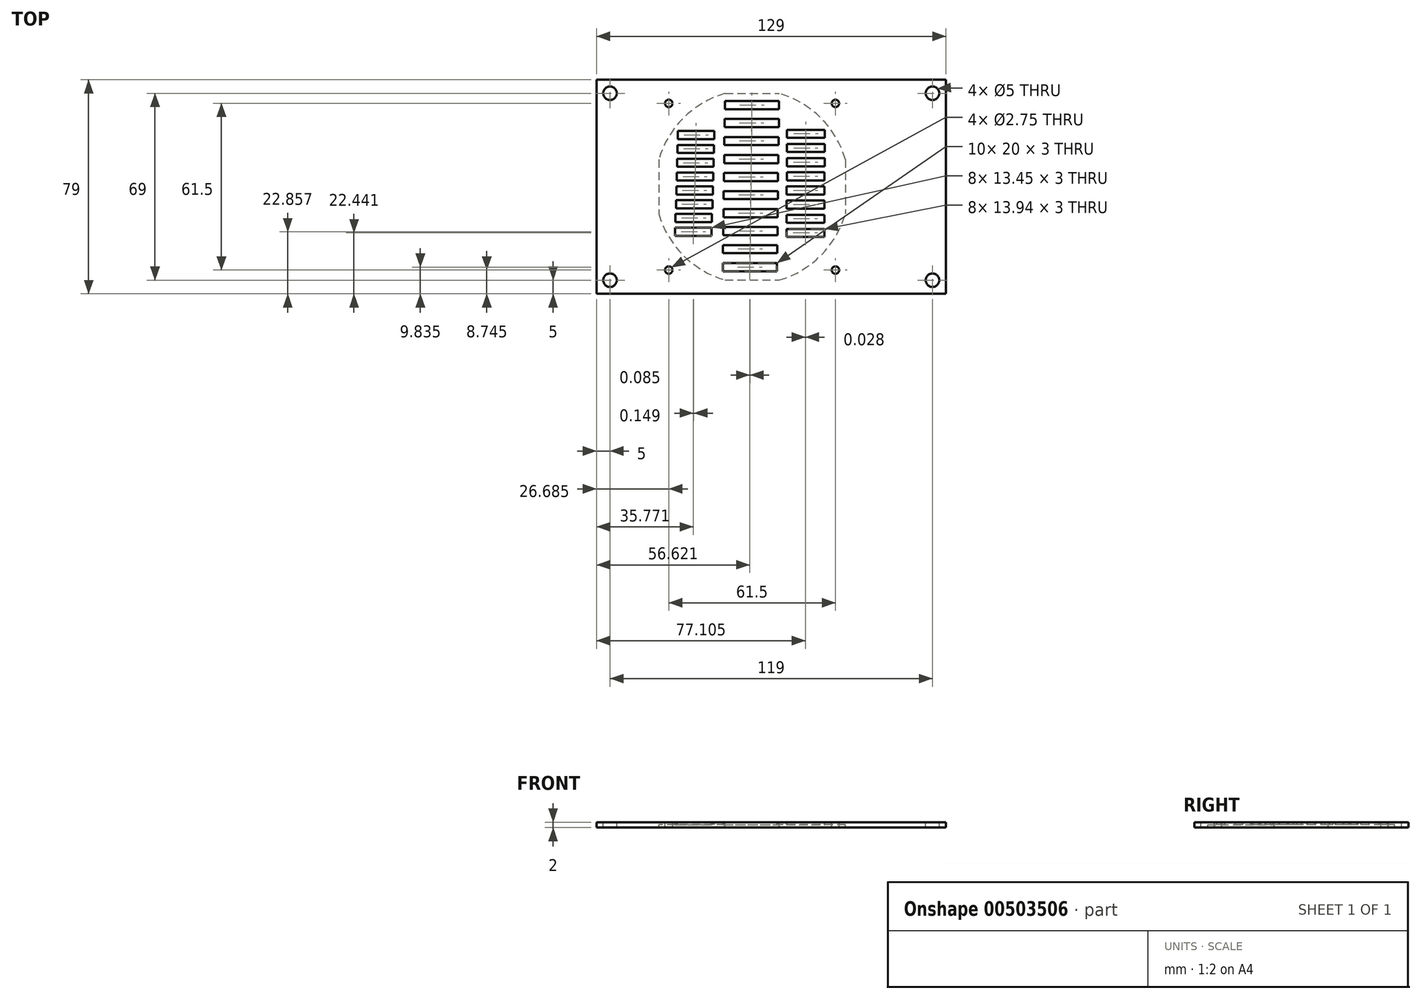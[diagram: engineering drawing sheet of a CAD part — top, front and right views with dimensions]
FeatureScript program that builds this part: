
annotation { "Feature Type Name" : "Feature", "Feature Type Description" : "" }
export const myFeature = defineFeature(function(context is Context, id is Id, definition is map)
    precondition{}
    {
        {
            var Q0;
            Q0=qCreatedBy(makeId("Top.planeOp"),FACE);
            var sketch = newSketch(context, id + "F0", { "sketchPlane" : qUnion([Q0])});
            skLineSegment(sketch, "E0.bottom", {"start": v(0, 0) * mm, "end": v(129, 0) * mm});
            skLineSegment(sketch, "E0.top", {"start": v(0, 79) * mm, "end": v(129, 79) * mm});
            skLineSegment(sketch, "E0.left", {"start": v(0, 0) * mm, "end": v(0, 79) * mm});
            skLineSegment(sketch, "E0.right", {"start": v(129, 0) * mm, "end": v(129, 79) * mm});
            skCircle(sketch, "E1", {"center": v(5, 74) * mm, "radius": 2.5 * mm});
            skCircle(sketch, "E2", {"center": v(124, 74) * mm, "radius": 2.5 * mm});
            skCircle(sketch, "E3", {"center": v(124, 5) * mm, "radius": 2.5 * mm});
            skCircle(sketch, "E4", {"center": v(5, 5) * mm, "radius": 2.5 * mm});
            skLineSegment(sketch, "E5.bottom", {"start": v(47.43, 73.93) * mm, "end": v(67.44, 73.93) * mm});
            skLineSegment(sketch, "E5.top", {"start": v(47.43, 5.06) * mm, "end": v(67.44, 5.06) * mm});
            skLineSegment(sketch, "E5.left", {"start": v(23, 49.5) * mm, "end": v(23, 29.49) * mm});
            skLineSegment(sketch, "E5.right", {"start": v(93.24, 41.52) * mm, "end": v(93.24, 41.52) * mm});
            skArc(sketch, "E6", {"start": v(23, 29.49) * mm, "mid": v(32.08, 14.14) * mm, "end": v(47.43, 5.06) * mm});
            skArc(sketch, "E7.trimOffspring", {"start": v(91.87, 49.5) * mm, "mid": v(82.8, 64.85) * mm, "end": v(67.44, 73.93) * mm});
            skArc(sketch, "E8.trimOffspring", {"start": v(47.43, 73.93) * mm, "mid": v(32.08, 64.85) * mm, "end": v(23, 49.5) * mm});
            skArc(sketch, "E9.trimOffspring", {"start": v(67.44, 5.06) * mm, "mid": v(82.8, 14.14) * mm, "end": v(91.87, 29.49) * mm});
            skLineSegment(sketch, "E10.bottom", {"start": v(16.58, 79) * mm, "end": v(98.29, 79) * mm});
            skLineSegment(sketch, "E10.top", {"start": v(16.58, 0) * mm, "end": v(98.29, 0) * mm});
            skLineSegment(sketch, "E10.left", {"start": v(16.58, 79) * mm, "end": v(16.58, 0) * mm});
            skLineSegment(sketch, "E10.right", {"start": v(98.29, 79) * mm, "end": v(98.29, 0) * mm});
            skCircle(sketch, "E11", {"center": v(26.68, 70.25) * mm, "radius": 1.38 * mm});
            skCircle(sketch, "E12", {"center": v(88.18, 70.25) * mm, "radius": 1.38 * mm});
            skCircle(sketch, "E13", {"center": v(88.19, 8.75) * mm, "radius": 1.38 * mm});
            skCircle(sketch, "E14", {"center": v(26.68, 8.75) * mm, "radius": 1.38 * mm});
            skPoint(sketch, "E15.firstSnap0", {"position": v(32.08, 14.14) * mm});
            skPoint(sketch, "E15.oppositeSnap0", {"position": v(86.71, 18.79) * mm});
            skLineSegment(sketch, "E16", {"start": v(91.87, 49.5) * mm, "end": v(91.87, 29.49) * mm});
            skLineSegment(sketch, "E17.bottom", {"start": v(47.38, 71.15) * mm, "end": v(67.38, 71.15) * mm});
            skLineSegment(sketch, "E17.top", {"start": v(47.38, 68.15) * mm, "end": v(67.38, 68.15) * mm});
            skLineSegment(sketch, "E17.left", {"start": v(47.38, 71.15) * mm, "end": v(47.38, 68.15) * mm});
            skLineSegment(sketch, "E17.right", {"start": v(67.38, 71.15) * mm, "end": v(67.38, 68.15) * mm});
            skLineSegment(sketch, "E18.1.0.0", {"start": v(47.3, 64.5) * mm, "end": v(67.3, 64.5) * mm});
            skLineSegment(sketch, "E18.1.0.1", {"start": v(47.3, 61.5) * mm, "end": v(67.3, 61.5) * mm});
            skLineSegment(sketch, "E18.1.0.2", {"start": v(47.3, 64.5) * mm, "end": v(47.3, 61.5) * mm});
            skLineSegment(sketch, "E18.1.0.3", {"start": v(67.3, 64.5) * mm, "end": v(67.3, 61.5) * mm});
            skLineSegment(sketch, "E18.2.0.0", {"start": v(47.22, 57.85) * mm, "end": v(67.22, 57.85) * mm});
            skLineSegment(sketch, "E18.2.0.1", {"start": v(47.22, 54.85) * mm, "end": v(67.22, 54.85) * mm});
            skLineSegment(sketch, "E18.2.0.2", {"start": v(47.22, 57.85) * mm, "end": v(47.22, 54.85) * mm});
            skLineSegment(sketch, "E18.2.0.3", {"start": v(67.22, 57.85) * mm, "end": v(67.22, 54.85) * mm});
            skLineSegment(sketch, "E18.3.0.0", {"start": v(47.13, 51.2) * mm, "end": v(67.13, 51.2) * mm});
            skLineSegment(sketch, "E18.3.0.1", {"start": v(47.13, 48.2) * mm, "end": v(67.13, 48.2) * mm});
            skLineSegment(sketch, "E18.3.0.2", {"start": v(47.13, 51.2) * mm, "end": v(47.13, 48.2) * mm});
            skLineSegment(sketch, "E18.3.0.3", {"start": v(67.13, 51.2) * mm, "end": v(67.13, 48.2) * mm});
            skLineSegment(sketch, "E18.4.0.0", {"start": v(47.05, 44.56) * mm, "end": v(67.05, 44.56) * mm});
            skLineSegment(sketch, "E18.4.0.1", {"start": v(47.05, 41.56) * mm, "end": v(67.05, 41.56) * mm});
            skLineSegment(sketch, "E18.4.0.2", {"start": v(47.05, 44.56) * mm, "end": v(47.05, 41.56) * mm});
            skLineSegment(sketch, "E18.4.0.3", {"start": v(67.05, 44.56) * mm, "end": v(67.05, 41.56) * mm});
            skLineSegment(sketch, "E18.5.0.0", {"start": v(46.96, 37.92) * mm, "end": v(66.96, 37.92) * mm});
            skLineSegment(sketch, "E18.5.0.1", {"start": v(46.96, 34.92) * mm, "end": v(66.96, 34.92) * mm});
            skLineSegment(sketch, "E18.5.0.2", {"start": v(46.96, 37.92) * mm, "end": v(46.96, 34.92) * mm});
            skLineSegment(sketch, "E18.5.0.3", {"start": v(66.96, 37.92) * mm, "end": v(66.96, 34.92) * mm});
            skLineSegment(sketch, "E18.6.0.0", {"start": v(46.88, 31.27) * mm, "end": v(66.88, 31.27) * mm});
            skLineSegment(sketch, "E18.6.0.1", {"start": v(46.88, 28.27) * mm, "end": v(66.88, 28.27) * mm});
            skLineSegment(sketch, "E18.6.0.2", {"start": v(46.88, 31.27) * mm, "end": v(46.88, 28.27) * mm});
            skLineSegment(sketch, "E18.6.0.3", {"start": v(66.88, 31.27) * mm, "end": v(66.88, 28.27) * mm});
            skLineSegment(sketch, "E18.7.0.0", {"start": v(46.8, 24.63) * mm, "end": v(66.8, 24.63) * mm});
            skLineSegment(sketch, "E18.7.0.1", {"start": v(46.8, 21.63) * mm, "end": v(66.8, 21.63) * mm});
            skLineSegment(sketch, "E18.7.0.2", {"start": v(46.8, 24.63) * mm, "end": v(46.8, 21.63) * mm});
            skLineSegment(sketch, "E18.7.0.3", {"start": v(66.8, 24.63) * mm, "end": v(66.8, 21.63) * mm});
            skLineSegment(sketch, "E18.8.0.0", {"start": v(46.7, 17.98) * mm, "end": v(66.7, 17.98) * mm});
            skLineSegment(sketch, "E18.8.0.1", {"start": v(46.7, 14.98) * mm, "end": v(66.7, 14.98) * mm});
            skLineSegment(sketch, "E18.8.0.2", {"start": v(46.7, 17.98) * mm, "end": v(46.7, 14.98) * mm});
            skLineSegment(sketch, "E18.8.0.3", {"start": v(66.7, 17.98) * mm, "end": v(66.7, 14.98) * mm});
            skLineSegment(sketch, "E18.9.0.0", {"start": v(46.62, 11.34) * mm, "end": v(66.62, 11.34) * mm});
            skLineSegment(sketch, "E18.9.0.1", {"start": v(46.62, 8.34) * mm, "end": v(66.62, 8.34) * mm});
            skLineSegment(sketch, "E18.9.0.2", {"start": v(46.62, 11.34) * mm, "end": v(46.62, 8.34) * mm});
            skLineSegment(sketch, "E18.9.0.3", {"start": v(66.62, 11.34) * mm, "end": v(66.62, 8.34) * mm});
            skLineSegment(sketch, "E18.direction1", {"start": v(47.38, 68.15) * mm, "end": v(47.3, 61.5) * mm, "construction": true});
            skLineSegment(sketch, "E19.bottom", {"start": v(30.09, 60.04) * mm, "end": v(43.54, 60.04) * mm});
            skLineSegment(sketch, "E19.top", {"start": v(30.09, 57.04) * mm, "end": v(43.54, 57.04) * mm});
            skLineSegment(sketch, "E19.left", {"start": v(30.09, 60.04) * mm, "end": v(30.09, 57.04) * mm});
            skLineSegment(sketch, "E19.right", {"start": v(43.54, 60.04) * mm, "end": v(43.54, 57.04) * mm});
            skLineSegment(sketch, "E20.1.0.0", {"start": v(29.94, 51.94) * mm, "end": v(43.39, 51.94) * mm});
            skLineSegment(sketch, "E20.1.0.1", {"start": v(29.94, 54.94) * mm, "end": v(43.39, 54.94) * mm});
            skLineSegment(sketch, "E20.1.0.2", {"start": v(43.39, 54.94) * mm, "end": v(43.39, 51.94) * mm});
            skLineSegment(sketch, "E20.1.0.3", {"start": v(29.94, 54.94) * mm, "end": v(29.94, 51.94) * mm});
            skLineSegment(sketch, "E20.2.0.0", {"start": v(29.79, 46.85) * mm, "end": v(43.24, 46.85) * mm});
            skLineSegment(sketch, "E20.2.0.1", {"start": v(29.79, 49.85) * mm, "end": v(43.24, 49.85) * mm});
            skLineSegment(sketch, "E20.2.0.2", {"start": v(43.24, 49.85) * mm, "end": v(43.24, 46.85) * mm});
            skLineSegment(sketch, "E20.2.0.3", {"start": v(29.79, 49.85) * mm, "end": v(29.79, 46.85) * mm});
            skLineSegment(sketch, "E20.3.0.0", {"start": v(29.64, 41.75) * mm, "end": v(43.1, 41.75) * mm});
            skLineSegment(sketch, "E20.3.0.1", {"start": v(29.64, 44.75) * mm, "end": v(43.1, 44.75) * mm});
            skLineSegment(sketch, "E20.3.0.2", {"start": v(43.1, 44.75) * mm, "end": v(43.1, 41.75) * mm});
            skLineSegment(sketch, "E20.3.0.3", {"start": v(29.64, 44.75) * mm, "end": v(29.64, 41.75) * mm});
            skLineSegment(sketch, "E20.4.0.0", {"start": v(29.5, 36.65) * mm, "end": v(42.94, 36.65) * mm});
            skLineSegment(sketch, "E20.4.0.1", {"start": v(29.5, 39.65) * mm, "end": v(42.94, 39.65) * mm});
            skLineSegment(sketch, "E20.4.0.2", {"start": v(42.94, 39.65) * mm, "end": v(42.94, 36.65) * mm});
            skLineSegment(sketch, "E20.4.0.3", {"start": v(29.5, 39.65) * mm, "end": v(29.5, 36.65) * mm});
            skLineSegment(sketch, "E20.5.0.0", {"start": v(29.34, 31.55) * mm, "end": v(42.8, 31.55) * mm});
            skLineSegment(sketch, "E20.5.0.1", {"start": v(29.34, 34.55) * mm, "end": v(42.8, 34.55) * mm});
            skLineSegment(sketch, "E20.5.0.2", {"start": v(42.8, 34.55) * mm, "end": v(42.8, 31.55) * mm});
            skLineSegment(sketch, "E20.5.0.3", {"start": v(29.34, 34.55) * mm, "end": v(29.34, 31.55) * mm});
            skLineSegment(sketch, "E20.6.0.0", {"start": v(29.2, 26.45) * mm, "end": v(42.65, 26.45) * mm});
            skLineSegment(sketch, "E20.6.0.1", {"start": v(29.2, 29.45) * mm, "end": v(42.65, 29.45) * mm});
            skLineSegment(sketch, "E20.6.0.2", {"start": v(42.65, 29.45) * mm, "end": v(42.65, 26.45) * mm});
            skLineSegment(sketch, "E20.6.0.3", {"start": v(29.2, 29.45) * mm, "end": v(29.2, 26.45) * mm});
            skLineSegment(sketch, "E20.7.0.0", {"start": v(29.04, 21.36) * mm, "end": v(42.5, 21.36) * mm});
            skLineSegment(sketch, "E20.7.0.1", {"start": v(29.04, 24.36) * mm, "end": v(42.5, 24.36) * mm});
            skLineSegment(sketch, "E20.7.0.2", {"start": v(42.5, 24.36) * mm, "end": v(42.5, 21.36) * mm});
            skLineSegment(sketch, "E20.7.0.3", {"start": v(29.04, 24.36) * mm, "end": v(29.04, 21.36) * mm});
            skLineSegment(sketch, "E20.direction1", {"start": v(30.09, 57.04) * mm, "end": v(29.94, 51.94) * mm, "construction": true});
            skLineSegment(sketch, "E21.bottom", {"start": v(70.33, 60.53) * mm, "end": v(84.27, 60.53) * mm});
            skLineSegment(sketch, "E21.top", {"start": v(70.33, 57.53) * mm, "end": v(84.27, 57.53) * mm});
            skLineSegment(sketch, "E21.left", {"start": v(70.33, 60.53) * mm, "end": v(70.33, 57.53) * mm});
            skLineSegment(sketch, "E21.right", {"start": v(84.27, 60.53) * mm, "end": v(84.27, 57.53) * mm});
            skLineSegment(sketch, "E22.1.0.0", {"start": v(84.24, 55.3) * mm, "end": v(84.24, 52.3) * mm});
            skLineSegment(sketch, "E22.1.0.1", {"start": v(70.3, 52.3) * mm, "end": v(84.24, 52.3) * mm});
            skLineSegment(sketch, "E22.1.0.2", {"start": v(70.3, 55.3) * mm, "end": v(70.3, 52.3) * mm});
            skLineSegment(sketch, "E22.1.0.3", {"start": v(70.3, 55.3) * mm, "end": v(84.24, 55.3) * mm});
            skLineSegment(sketch, "E22.2.0.0", {"start": v(84.21, 50.07) * mm, "end": v(84.21, 47.07) * mm});
            skLineSegment(sketch, "E22.2.0.1", {"start": v(70.27, 47.07) * mm, "end": v(84.21, 47.07) * mm});
            skLineSegment(sketch, "E22.2.0.2", {"start": v(70.27, 50.07) * mm, "end": v(70.27, 47.07) * mm});
            skLineSegment(sketch, "E22.2.0.3", {"start": v(70.27, 50.07) * mm, "end": v(84.21, 50.07) * mm});
            skLineSegment(sketch, "E22.3.0.0", {"start": v(84.18, 44.85) * mm, "end": v(84.18, 41.85) * mm});
            skLineSegment(sketch, "E22.3.0.1", {"start": v(70.24, 41.85) * mm, "end": v(84.18, 41.85) * mm});
            skLineSegment(sketch, "E22.3.0.2", {"start": v(70.24, 44.85) * mm, "end": v(70.24, 41.85) * mm});
            skLineSegment(sketch, "E22.3.0.3", {"start": v(70.24, 44.85) * mm, "end": v(84.18, 44.85) * mm});
            skLineSegment(sketch, "E22.4.0.0", {"start": v(84.16, 39.62) * mm, "end": v(84.16, 36.62) * mm});
            skLineSegment(sketch, "E22.4.0.1", {"start": v(70.22, 36.62) * mm, "end": v(84.16, 36.62) * mm});
            skLineSegment(sketch, "E22.4.0.2", {"start": v(70.22, 39.62) * mm, "end": v(70.22, 36.62) * mm});
            skLineSegment(sketch, "E22.4.0.3", {"start": v(70.22, 39.62) * mm, "end": v(84.16, 39.62) * mm});
            skLineSegment(sketch, "E22.5.0.0", {"start": v(84.13, 34.4) * mm, "end": v(84.13, 31.4) * mm});
            skLineSegment(sketch, "E22.5.0.1", {"start": v(70.19, 31.4) * mm, "end": v(84.13, 31.4) * mm});
            skLineSegment(sketch, "E22.5.0.2", {"start": v(70.19, 34.4) * mm, "end": v(70.19, 31.4) * mm});
            skLineSegment(sketch, "E22.5.0.3", {"start": v(70.19, 34.4) * mm, "end": v(84.13, 34.4) * mm});
            skLineSegment(sketch, "E22.6.0.0", {"start": v(84.1, 29.17) * mm, "end": v(84.1, 26.17) * mm});
            skLineSegment(sketch, "E22.6.0.1", {"start": v(70.16, 26.17) * mm, "end": v(84.1, 26.17) * mm});
            skLineSegment(sketch, "E22.6.0.2", {"start": v(70.16, 29.17) * mm, "end": v(70.16, 26.17) * mm});
            skLineSegment(sketch, "E22.6.0.3", {"start": v(70.16, 29.17) * mm, "end": v(84.1, 29.17) * mm});
            skLineSegment(sketch, "E22.7.0.0", {"start": v(84.07, 23.94) * mm, "end": v(84.07, 20.94) * mm});
            skLineSegment(sketch, "E22.7.0.1", {"start": v(70.13, 20.94) * mm, "end": v(84.07, 20.94) * mm});
            skLineSegment(sketch, "E22.7.0.2", {"start": v(70.13, 23.94) * mm, "end": v(70.13, 20.94) * mm});
            skLineSegment(sketch, "E22.7.0.3", {"start": v(70.13, 23.94) * mm, "end": v(84.07, 23.94) * mm});
            skLineSegment(sketch, "E22.direction1", {"start": v(70.33, 57.53) * mm, "end": v(70.3, 52.3) * mm, "construction": true});
            skSolve(sketch);
        }
        {
            var Q0;
            {var subQ0=sQuery(id+"F0.wireOp",EDGE,"E0.left");Q0=makeQuery(id+"F0.imprint","IMPRINT",FACE,{"disambiguationData":[TD([[makeQuery(id+"F0.imprint","IMPRINT",EDGE,{"derivedFrom":subQ0}),-1.0]])]});}
            var Q1;
            Q1=makeQuery(id+"F0.imprint","IMPRINT",FACE,{"disambiguationData":[TD([[makeQuery(id+"F0.imprint","IMPRINT",EDGE,{"derivedFrom":sQuery(id+"F0.wireOp",EDGE,"E5.bottom")}),1.0]])]});
            var Q2;
            {var subQ0=sQuery(id+"F0.wireOp",EDGE,"E0.right");Q2=makeQuery(id+"F0.imprint","IMPRINT",FACE,{"disambiguationData":[TD([[makeQuery(id+"F0.imprint","IMPRINT",EDGE,{"derivedFrom":subQ0}),1.0]])]});}
            extrude(context, id + "F1", {"entities" : qUnion([Q0, Q1, Q2]), "oppositeDirection" : true, "depth" : 2 * mm});
        }
        {
            var Q0;
            Q0=makeQuery(id+"F0.imprint","IMPRINT",FACE,{"disambiguationData":[TD([[makeQuery(id+"F0.imprint","IMPRINT",EDGE,{"derivedFrom":sQuery(id+"F0.wireOp",EDGE,"E5.bottom")}),-1.0]])]});
            extrude(context, id + "F2", {"entities" : qUnion([Q0]), "operationType" : NewBodyOperationType.ADD, "oppositeDirection" : true, "depth" : 1 * mm, "hasSecondDirection" : true, "secondDirectionOppositeDirection" : false, "secondDirectionDepth" : 0 * mm});
        }
    });
